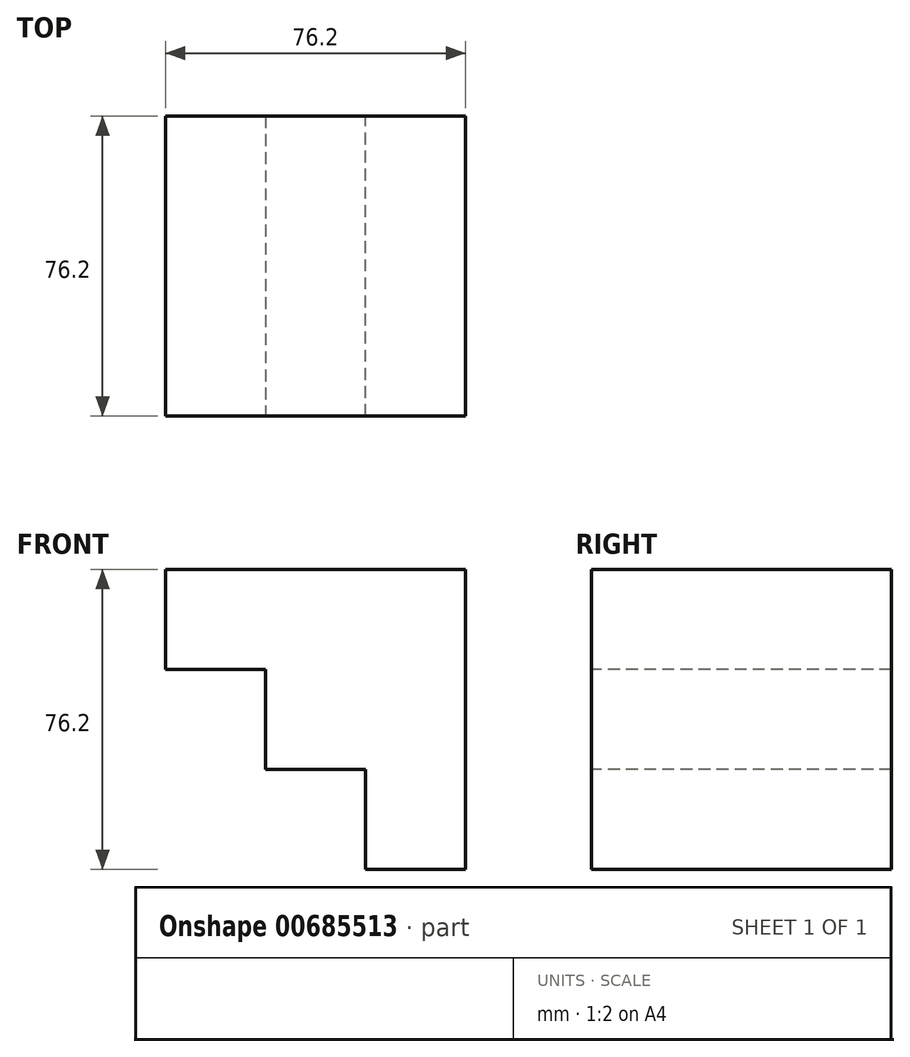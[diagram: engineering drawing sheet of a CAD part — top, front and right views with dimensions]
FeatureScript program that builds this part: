
annotation { "Feature Type Name" : "Feature", "Feature Type Description" : "" }
export const myFeature = defineFeature(function(context is Context, id is Id, definition is map)
    precondition{}
    {
        {
            var Q0;
            Q0=qCreatedBy(makeId("Front.planeOp"),FACE);
            var sketch = newSketch(context, id + "F0", { "sketchPlane" : qUnion([Q0])});
            skLineSegment(sketch, "E0.bottom", {"start": v(0, 0) * mm, "end": v(76.2, 0) * mm});
            skLineSegment(sketch, "E0.top", {"start": v(0, 76.2) * mm, "end": v(76.2, 76.2) * mm});
            skLineSegment(sketch, "E0.left", {"start": v(0, 0) * mm, "end": v(0, 76.2) * mm});
            skLineSegment(sketch, "E0.right", {"start": v(76.2, 0) * mm, "end": v(76.2, 76.2) * mm});
            skSolve(sketch);
        }
        {
            var Q0;
            Q0=qCreatedBy(makeId("Front.planeOp"),FACE);
            var sketch = newSketch(context, id + "F1", { "sketchPlane" : qUnion([Q0])});
            skLineSegment(sketch, "E1.bottom", {"start": v(0, 0) * mm, "end": v(50.8, 0) * mm});
            skLineSegment(sketch, "E1.top", {"start": v(0, 25.4) * mm, "end": v(50.8, 25.4) * mm});
            skLineSegment(sketch, "E1.left", {"start": v(0, 0) * mm, "end": v(0, 25.4) * mm});
            skLineSegment(sketch, "E1.right", {"start": v(50.8, 0) * mm, "end": v(50.8, 25.4) * mm});
            skSolve(sketch);
        }
        {
            var Q0;
            Q0 = qSketchRegion(id + "F0", true);
            extrude(context, id + "F2", {"entities" : qUnion([Q0]), "depth" : 76.2 * mm, "offsetDistance" : 25.4 * mm});
        }
        {
            var Q0;
            Q0 = qSketchRegion(id + "F1", true);
            extrude(context, id + "F3", {"entities" : qUnion([Q0]), "operationType" : NewBodyOperationType.REMOVE, "depth" : 164.6 * mm, "offsetDistance" : 25.4 * mm});
        }
        {
            var Q0;
            Q0=makeQuery(id+"F2.opExtrude","CAP_FACE",FACE,{"disambiguationData":[OSD([sQuery(id+"F0.wireOp",EDGE,"E0.bottom"),sQuery(id+"F0.wireOp",EDGE,"E0.top"),sQuery(id+"F0.wireOp",EDGE,"E0.left"),sQuery(id+"F0.wireOp",EDGE,"E0.right")])],"isStart":false});
            var sketch = newSketch(context, id + "F4", { "sketchPlane" : qUnion([Q0])});
            skLineSegment(sketch, "E2.bottom", {"start": v(0, 25.4) * mm, "end": v(25.4, 25.4) * mm});
            skLineSegment(sketch, "E2.top", {"start": v(0, 50.8) * mm, "end": v(25.4, 50.8) * mm});
            skLineSegment(sketch, "E2.left", {"start": v(0, 25.4) * mm, "end": v(0, 50.8) * mm});
            skLineSegment(sketch, "E2.right", {"start": v(25.4, 25.4) * mm, "end": v(25.4, 50.8) * mm});
            skSolve(sketch);
        }
        {
            var Q0;
            Q0 = qSketchRegion(id + "F4", true);
            extrude(context, id + "F5", {"entities" : qUnion([Q0]), "operationType" : NewBodyOperationType.REMOVE, "oppositeDirection" : true, "depth" : 76.2 * mm, "offsetDistance" : 25.4 * mm});
        }
    });
